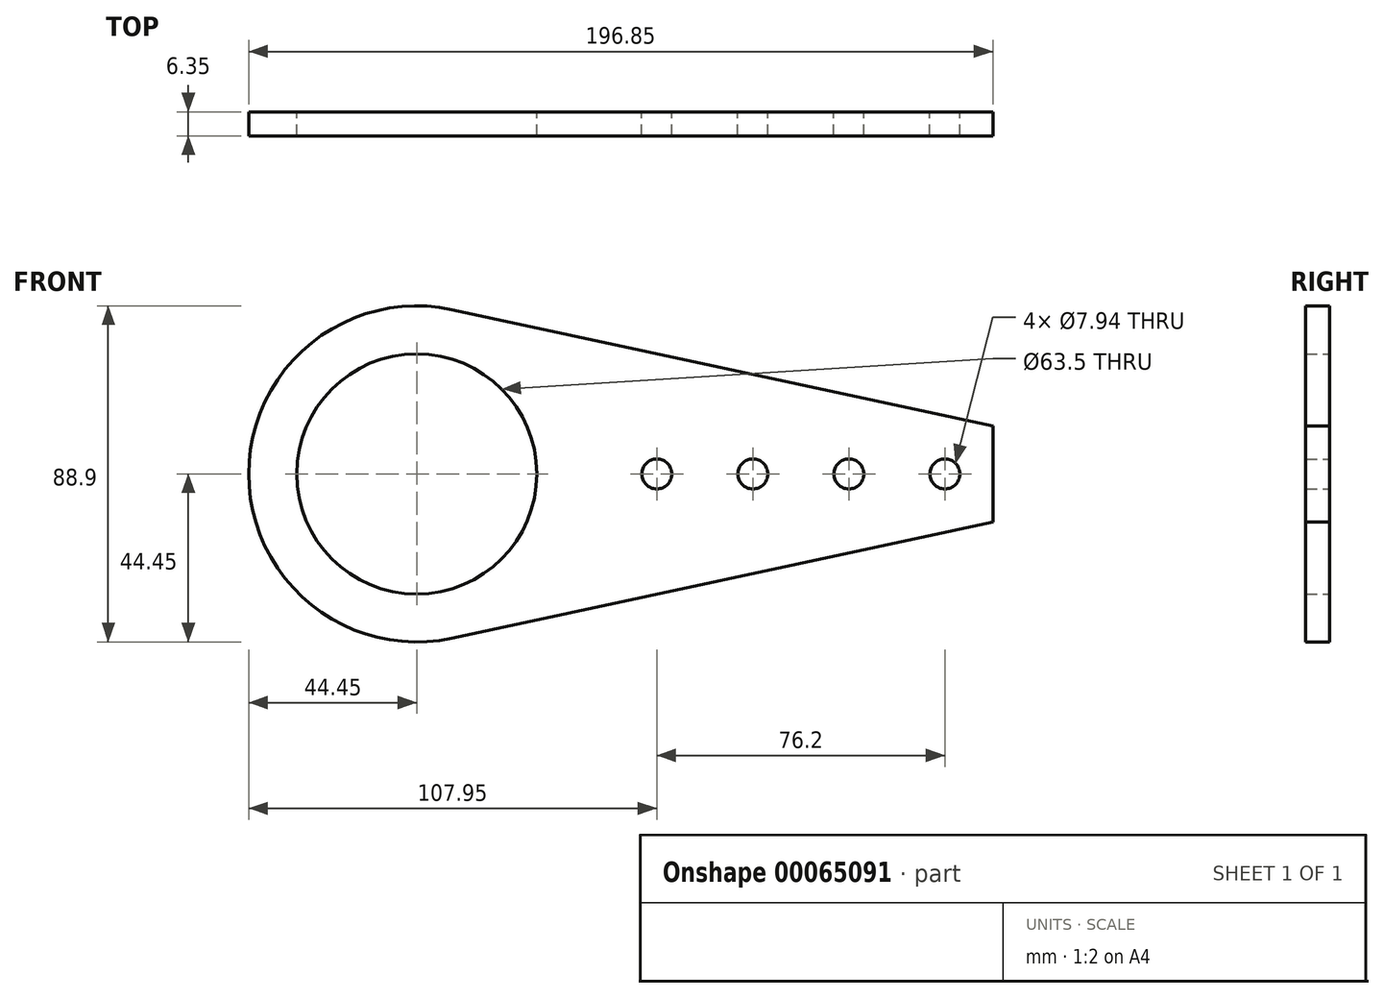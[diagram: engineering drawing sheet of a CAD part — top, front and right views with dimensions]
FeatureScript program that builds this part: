
annotation { "Feature Type Name" : "Feature", "Feature Type Description" : "" }
export const myFeature = defineFeature(function(context is Context, id is Id, definition is map)
    precondition{}
    {
        {
            var Q0;
            Q0=qCreatedBy(makeId("Front.planeOp"),FACE);
            var sketch = newSketch(context, id + "F0", { "sketchPlane" : qUnion([Q0])});
            skCircle(sketch, "E0", {"center": v(0, 0) * mm, "radius": 31.75 * mm});
            skCircle(sketch, "E1", {"center": v(0, 0) * mm, "radius": 44.45 * mm});
            skLineSegment(sketch, "E2", {"start": v(-52.66, 0) * mm, "end": v(161.01, 0) * mm, "construction": true});
            skLineSegment(sketch, "E3", {"start": v(152.4, 0) * mm, "end": v(152.4, 12.7) * mm});
            skLineSegment(sketch, "E4", {"start": v(152.4, 0) * mm, "end": v(152.4, -12.7) * mm});
            skLineSegment(sketch, "E5", {"start": v(9.34, 43.46) * mm, "end": v(152.4, 12.7) * mm});
            skLineSegment(sketch, "E6", {"start": v(9.34, -43.46) * mm, "end": v(152.4, -12.7) * mm});
            skCircle(sketch, "E7", {"center": v(139.7, 0) * mm, "radius": 3.97 * mm});
            skCircle(sketch, "E8", {"center": v(114.3, 0) * mm, "radius": 3.97 * mm});
            skCircle(sketch, "E9", {"center": v(88.9, 0) * mm, "radius": 3.97 * mm});
            skCircle(sketch, "E10", {"center": v(63.5, 0) * mm, "radius": 3.97 * mm});
            skSolve(sketch);
        }
        {
            var Q0;
            Q0=makeQuery(id+"F0.imprint","IMPRINT",FACE,{"disambiguationData":[TD([[makeQuery(id+"F0.imprint","IMPRINT",EDGE,{"derivedFrom":sQuery(id+"F0.wireOp",EDGE,"E0")}),-1.0]])]});
            var Q1;
            Q1=makeQuery(id+"F0.imprint","IMPRINT",FACE,{"disambiguationData":[TD([[makeQuery(id+"F0.imprint","IMPRINT",EDGE,{"derivedFrom":sQuery(id+"F0.wireOp",EDGE,"E3")}),1.0]])]});
            extrude(context, id + "F1", {"entities" : qUnion([Q0, Q1]), "depth" : 6.35 * mm});
        }
    });
